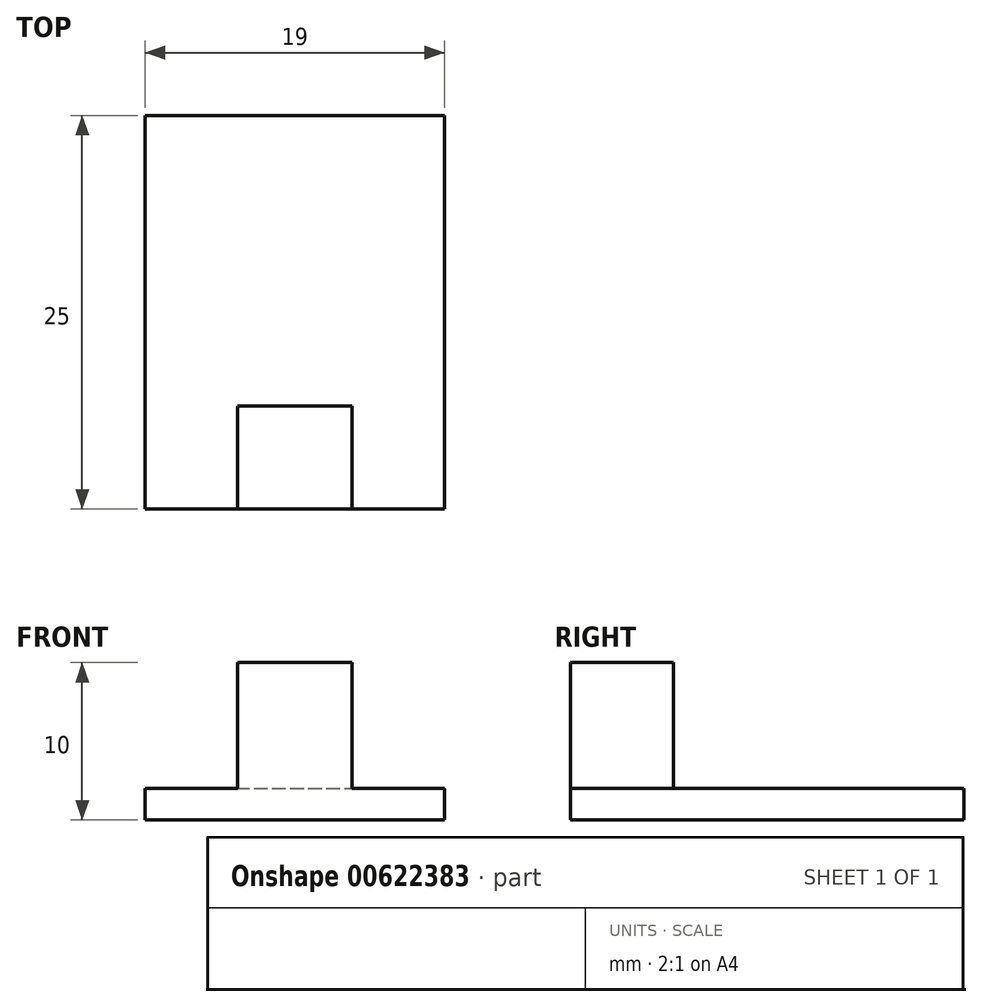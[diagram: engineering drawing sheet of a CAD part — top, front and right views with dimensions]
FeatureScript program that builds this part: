
annotation { "Feature Type Name" : "Feature", "Feature Type Description" : "" }
export const myFeature = defineFeature(function(context is Context, id is Id, definition is map)
    precondition{}
    {
        {
            var Q0;
            Q0=qCreatedBy(makeId("Top.planeOp"),FACE);
            var sketch = newSketch(context, id + "F0", { "sketchPlane" : qUnion([Q0])});
            skLineSegment(sketch, "E0.bottom", {"start": v(-9.5, 25) * mm, "end": v(9.5, 25) * mm});
            skLineSegment(sketch, "E0.top", {"start": v(-9.5, 0) * mm, "end": v(9.5, 0) * mm});
            skLineSegment(sketch, "E0.left", {"start": v(-9.5, 25) * mm, "end": v(-9.5, 0) * mm});
            skLineSegment(sketch, "E0.right", {"start": v(9.5, 25) * mm, "end": v(9.5, 0) * mm});
            skPoint(sketch, "E1", {"position": v(0, 25) * mm});
            skSolve(sketch);
        }
        {
            var Q0;
            Q0 = qSketchRegion(id + "F0", true);
            extrude(context, id + "F1", {"entities" : qUnion([Q0]), "depth" : 2 * mm, "offsetDistance" : 25 * mm});
        }
        {
            var Q0;
            Q0=makeQuery(id+"F1.opExtrude","CAP_FACE",FACE,{"disambiguationData":[OSD([sQuery(id+"F0.wireOp",EDGE,"E0.bottom"),sQuery(id+"F0.wireOp",EDGE,"E0.top"),sQuery(id+"F0.wireOp",EDGE,"E0.left"),sQuery(id+"F0.wireOp",EDGE,"E0.right")])],"isStart":false});
            var sketch = newSketch(context, id + "F2", { "sketchPlane" : qUnion([Q0])});
            skLineSegment(sketch, "E2.bottom", {"start": v(-3.63, 0) * mm, "end": v(3.63, 0) * mm});
            skLineSegment(sketch, "E2.top", {"start": v(-3.63, 6.55) * mm, "end": v(3.63, 6.55) * mm});
            skLineSegment(sketch, "E2.left", {"start": v(-3.63, 0) * mm, "end": v(-3.63, 6.55) * mm});
            skLineSegment(sketch, "E2.right", {"start": v(3.63, 0) * mm, "end": v(3.63, 6.55) * mm});
            skPoint(sketch, "E3", {"position": v(0, 0) * mm});
            skSolve(sketch);
        }
        {
            var Q0;
            Q0 = qSketchRegion(id + "F2", true);
            extrude(context, id + "F3", {"entities" : qUnion([Q0]), "operationType" : NewBodyOperationType.ADD, "depth" : 8 * mm, "offsetDistance" : 25 * mm});
        }
    });
